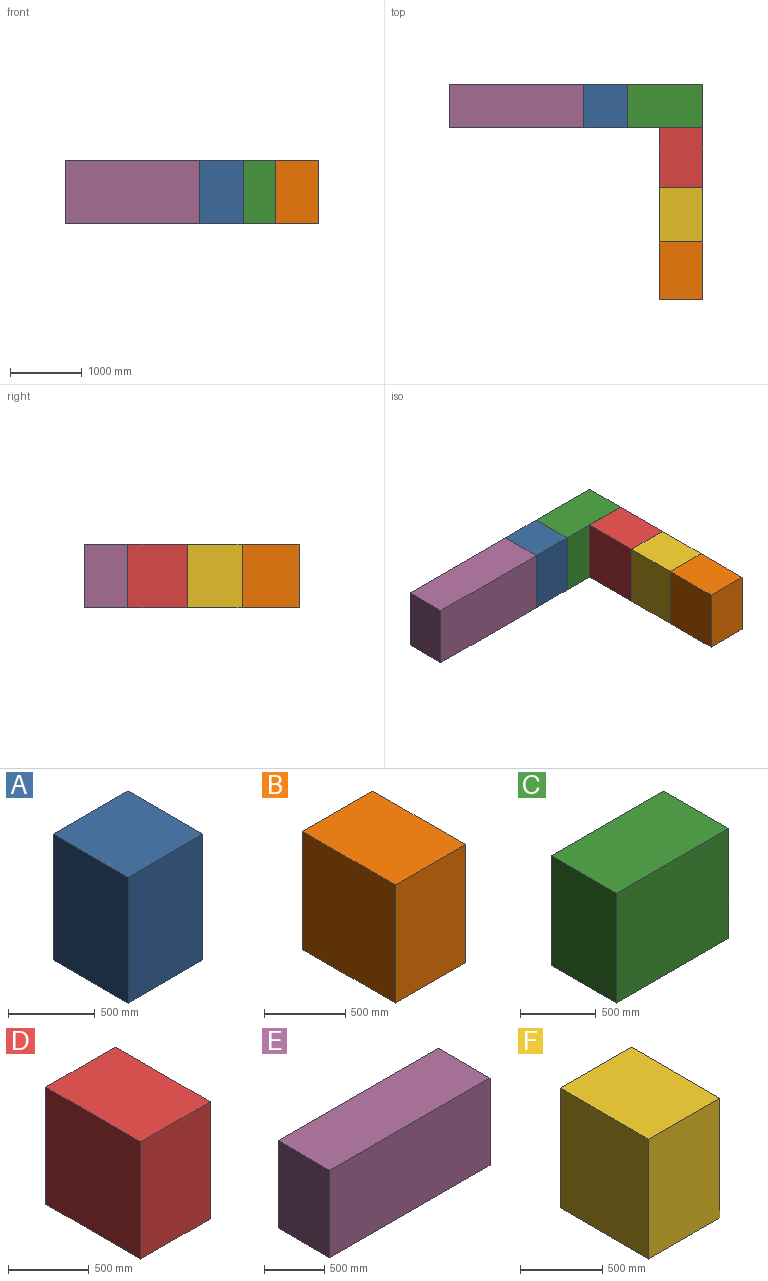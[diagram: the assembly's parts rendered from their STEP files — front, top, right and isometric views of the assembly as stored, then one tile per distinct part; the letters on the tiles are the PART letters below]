
ASSEMBLY  parts=6 mates=15
PART A: 6 faces, bbox 609.6x609.6x889 mm
  f0: plane 889x609.6mm, normal (-1,0,0), area 541934.4mm2, adj f1,f3,f4,f5
  f1: plane 889x609.6mm, normal (0,-1,0), area 541934.4mm2, adj f0,f2,f4,f5
  f2: plane 889x609.6mm, normal (1,0,0), area 541934.4mm2, adj f1,f3,f4,f5
  f3: plane 889x609.6mm, normal (0,1,0), area 541934.4mm2, adj f0,f2,f4,f5
  f4: plane 609.6x609.6mm, normal (0,0,1), area 371612.2mm2, adj f0,f1,f2,f3
  f5: plane 609.6x609.6mm, normal (0,0,-1), area 371612.2mm2, adj f0,f1,f2,f3
PART B: 6 faces, bbox 609.6x806.5x889 mm
  f0: plane 889x609.6mm, normal (0,1,0), area 541934.4mm2, adj f1,f3,f4,f5
  f1: plane 889x806.45mm, normal (-1,0,0), area 716934.1mm2, adj f0,f2,f4,f5
  f2: plane 889x609.6mm, normal (0,-1,0), area 541934.4mm2, adj f1,f3,f4,f5
  f3: plane 889x806.45mm, normal (1,0,0), area 716934.1mm2, adj f0,f2,f4,f5
  f4: plane 806.45x609.6mm, normal (0,0,1), area 491611.9mm2, adj f0,f1,f2,f3
  f5: plane 806.45x609.6mm, normal (0,0,-1), area 491611.9mm2, adj f0,f1,f2,f3
PART C: 6 faces, bbox 1050.9x609.6x889 mm
  f0: plane 889x609.6mm, normal (-1,0,0), area 541934.4mm2, adj f1,f3,f4,f5
  f1: plane 1050.93x889mm, normal (0,-1,0), area 934272.3mm2, adj f0,f2,f4,f5
  f2: plane 889x609.6mm, normal (1,0,0), area 541934.4mm2, adj f1,f3,f4,f5
  f3: plane 1050.93x889mm, normal (0,1,0), area 934272.3mm2, adj f0,f2,f4,f5
  f4: plane 1050.93x609.6mm, normal (0,0,1), area 640643.9mm2, adj f0,f1,f2,f3
  f5: plane 1050.93x609.6mm, normal (0,0,-1), area 640643.9mm2, adj f0,f1,f2,f3
PART D: 6 faces, bbox 609.6x831.9x889 mm
  f0: plane 889x609.6mm, normal (0,1,0), area 541934.4mm2, adj f1,f3,f4,f5
  f1: plane 889x831.85mm, normal (-1,0,0), area 739514.6mm2, adj f0,f2,f4,f5
  f2: plane 889x609.6mm, normal (0,-1,0), area 541934.4mm2, adj f1,f3,f4,f5
  f3: plane 889x831.85mm, normal (1,0,0), area 739514.6mm2, adj f0,f2,f4,f5
  f4: plane 831.85x609.6mm, normal (0,0,1), area 507095.8mm2, adj f0,f1,f2,f3
  f5: plane 831.85x609.6mm, normal (0,0,-1), area 507095.8mm2, adj f0,f1,f2,f3
PART E: 6 faces, bbox 1882.8x609.6x889 mm
  f0: plane 1882.78x889mm, normal (0,-1,0), area 1673787mm2, adj f1,f3,f4,f5
  f1: plane 889x609.6mm, normal (1,0,0), area 541934.4mm2, adj f0,f2,f4,f5
  f2: plane 1882.78x889mm, normal (0,1,0), area 1673787mm2, adj f1,f3,f4,f5
  f3: plane 889x609.6mm, normal (-1,0,0), area 541934.4mm2, adj f0,f2,f4,f5
  f4: plane 1882.78x609.6mm, normal (0,0,1), area 1147739.6mm2, adj f0,f1,f2,f3
  f5: plane 1882.78x609.6mm, normal (0,0,-1), area 1147739.6mm2, adj f0,f1,f2,f3
PART F: 6 faces, bbox 609.6x762x889 mm
  f0: plane 889x609.6mm, normal (0,1,0), area 541934.4mm2, adj f1,f3,f4,f5
  f1: plane 889x762mm, normal (-1,0,0), area 677418mm2, adj f0,f2,f4,f5
  f2: plane 889x609.6mm, normal (0,-1,0), area 541934.4mm2, adj f1,f3,f4,f5
  f3: plane 889x762mm, normal (1,0,0), area 677418mm2, adj f0,f2,f4,f5
  f4: plane 762x609.6mm, normal (0,0,1), area 464515.2mm2, adj f0,f1,f2,f3
  f5: plane 762x609.6mm, normal (0,0,-1), area 464515.2mm2, adj f0,f1,f2,f3
PLACE A t=(-3581.43,-588.99,-889)mm
PLACE B t=(815.59,-1150.81,-889)mm
PLACE C t=(-1050.92,-609.6,-889)mm
PLACE D t=(-1506.92,119.64,-889)mm
PLACE E t=(-692.19,-549.12,-889)mm
PLACE F t=(1.34,-549.99,-889)mm
MATE planar C.f3 <-> A.f3  axis (0,1,0) through (-525.46,0,-444.5)mm
MATE planar F.f0 <-> D.f2  axis (0,1,0) through (-304.8,-1441.45,-444.5)mm
MATE planar C.f1 <-> D.f0  axis (0,-1,0) through (-525.46,-609.6,-444.5)mm
MATE planar C.f3 <-> E.f2  axis (0,1,0) through (-525.46,0,-444.5)mm
MATE planar D.f3 <-> C.f2  axis (1,0,0) through (0,-1025.53,-444.5)mm
MATE planar E.f1 <-> A.f0  axis (1,0,0) through (-1660.52,-304.8,-444.5)mm
MATE planar C.f5 <-> A.f5  axis (0,0,-1) through (-525.46,-304.8,-889)mm
MATE planar C.f5 <-> F.f5  axis (0,0,-1) through (-525.46,-304.8,-889)mm
MATE planar B.f0 <-> F.f2  axis (0,1,0) through (-304.8,-2203.45,-444.5)mm
MATE planar D.f5 <-> C.f5  axis (0,0,-1) through (-304.8,-1025.53,-889)mm
MATE planar A.f2 <-> C.f0  axis (1,0,0) through (-1050.92,-304.8,-444.5)mm
MATE planar C.f2 <-> F.f3  axis (1,0,0) through (0,-304.8,-444.5)mm
MATE planar C.f2 <-> B.f3  axis (1,0,0) through (0,-304.8,-444.5)mm
MATE planar C.f5 <-> E.f5  axis (0,0,-1) through (-525.46,-304.8,-889)mm
MATE planar C.f5 <-> B.f5  axis (0,0,-1) through (-525.46,-304.8,-889)mm
